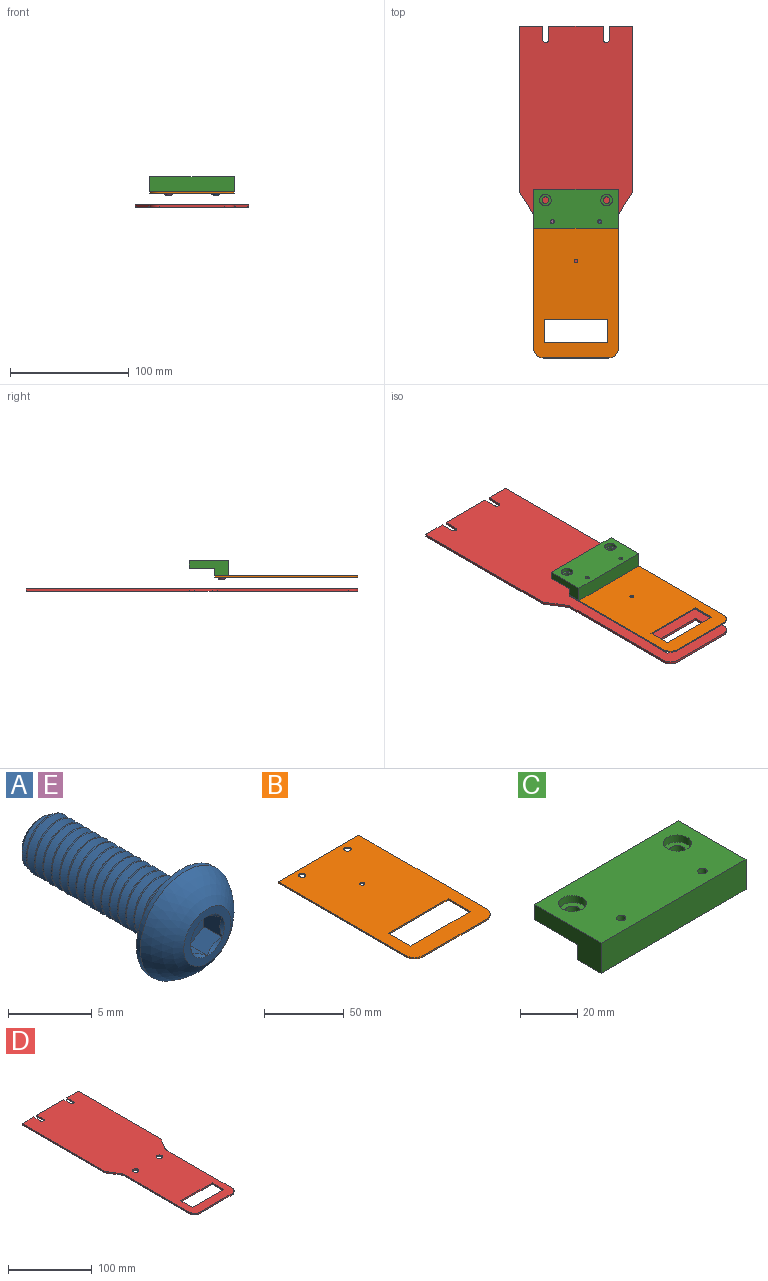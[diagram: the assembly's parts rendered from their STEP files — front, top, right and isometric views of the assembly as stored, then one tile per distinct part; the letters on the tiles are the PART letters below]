
ASSEMBLY  parts=5 mates=4
PART A: 24 faces, bbox 8.1x15x8.1 mm
  f0: cylinder r=2mm len=11.48mm, axis (0,1,0), area 2.5mm2, adj f2,f4,f6,f9
  f1: cone r=1.47mm half-angle=45deg, axis (0,-1,0), area 3.5mm2, adj f2,f3,f4,f5
  f2: cone r=1.47mm half-angle=45deg, axis (0,-1,0), area 0.9mm2, adj f0,f1,f4,f6
  f3: plane 2.95x2.95mm, normal (0,1,0), area 6.8mm2, adj f1
  f4: bspline ~12.61x4.62mm, area 97.8mm2, adj f0,f1,f2,f5,f9
  f5: cylinder r=1.55mm len=11.93mm, axis (0,1,0), area 17mm2, adj f1,f4,f6,f9
  f6: bspline ~12.4x4.62mm, area 97.9mm2, adj f0,f2,f5,f9
  f7: sphere r=4.23mm, area 49.7mm2, adj f8,f10
  f8: plane 4x4mm, normal (0,-1,0), area 6mm2, adj f7,f11,f12,f13,f14,f15,f16
  f9: plane 7.88x7.88mm, normal (0,1,0), area 35.4mm2, adj f0,f4,f5,f6,f10
  f10: cylinder r=3.8mm len=7.6mm, axis (0,-1,0), area 7.9mm2, adj f7,f9
  f11: cone r=1.44mm half-angle=45deg, axis (0,-1,0), area 0mm2, adj f8,f18
  f12: cone r=1.44mm half-angle=45deg, axis (0,-1,0), area 0mm2, adj f8,f19
  f13: cone r=1.44mm half-angle=45deg, axis (0,-1,0), area 0mm2, adj f8,f20
  f14: cone r=1.44mm half-angle=45deg, axis (0,-1,0), area 0mm2, adj f8,f21
  f15: cone r=1.44mm half-angle=45deg, axis (0,-1,0), area 0mm2, adj f8,f22
  f16: cone r=1.44mm half-angle=45deg, axis (0,-1,0), area 0mm2, adj f8,f23
  f17: plane 2.89x2.5mm, normal (0,-1,0), area 5.4mm2, adj f18,f19,f20,f21,f22,f23
  f18: plane 2.09x1.99mm, normal (-1,0,0), area 2mm2, adj f11,f17,f19,f23
  f19: plane 2.09x1.8mm, normal (-0.5,0,-0.87), area 2mm2, adj f12,f17,f18,f20
  f20: plane 2.09x1.8mm, normal (0.5,0,-0.87), area 2mm2, adj f13,f17,f19,f21
  f21: plane 2.09x1.99mm, normal (1,0,0), area 2mm2, adj f14,f17,f20,f22
  f22: plane 2.09x1.8mm, normal (0.5,0,0.87), area 2mm2, adj f15,f17,f21,f23
  f23: plane 2.09x1.8mm, normal (-0.5,0,0.87), area 2mm2, adj f16,f17,f18,f22
PART B: 15 faces, bbox 71.4x120.7x1 mm
  f0: plane 71.4x1mm, normal (0,1,0), area 71.4mm2, adj f1,f10,f11,f12
  f1: plane 112.7x1mm, normal (-1,0,0), area 112.7mm2, adj f0,f2,f11,f12
  f2: cylinder r=8mm len=8mm, axis (0,0,-1), area 12.6mm2, adj f1,f3,f11,f12
  f3: plane 55.4x1mm, normal (0,-1,0), area 55.4mm2, adj f2,f4,f11,f12
  f4: cylinder r=8mm len=8mm, axis (0,0,-1), area 12.6mm2, adj f3,f10,f11,f12
  f5: plane 52.8x1mm, normal (0,-1,0), area 52.8mm2, adj f6,f9,f11,f12
  f6: plane 19.6x1mm, normal (-1,0,0), area 19.6mm2, adj f5,f7,f11,f12
  f7: plane 52.8x1mm, normal (0,1,0), area 52.8mm2, adj f6,f9,f11,f12
  f8: cylinder r=1.5mm len=3mm, axis (0,0,-1), area 9.4mm2, adj f11,f12
  f9: plane 19.6x1mm, normal (1,0,0), area 19.6mm2, adj f5,f7,f11,f12
  f10: plane 112.7x1mm, normal (1,0,0), area 112.7mm2, adj f0,f4,f11,f12
  f11: plane 120.7x71.4mm, normal (0,0,1), area 7516.8mm2, adj f0,f1,f2,f3,f4,f5,f6,f7
  f12: plane 120.7x71.4mm, normal (0,0,-1), area 7516.8mm2, adj f0,f1,f2,f3,f4,f5,f6,f7
  f13: cylinder r=2.25mm len=4.5mm, axis (0,0,-1), area 14.1mm2, adj f11,f12
  f14: cylinder r=2.25mm len=4.5mm, axis (0,0,-1), area 14.1mm2, adj f11,f12
PART C: 16 faces, bbox 71.4x33x12.8 mm
  f0: plane 71.4x6.4mm, normal (0,1,0), area 457mm2, adj f1,f5,f6,f7
  f1: plane 71.4x21.5mm, normal (0,0,-1), area 1487.6mm2, adj f0,f2,f6,f7,f8,f11
  f2: plane 71.4x6.4mm, normal (0,1,0), area 457mm2, adj f1,f3,f6,f7
  f3: plane 71.4x33mm, normal (0,0,1), area 2189.8mm2, adj f2,f4,f6,f7,f10,f13,f14,f15
  f4: plane 71.4x12.8mm, normal (0,-1,0), area 913.9mm2, adj f3,f5,f6,f7
  f5: plane 71.4x11.5mm, normal (0,0,-1), area 804mm2, adj f0,f4,f6,f7,f14,f15
  f6: plane 33x12.8mm, normal (1,0,0), area 284.8mm2, adj f0,f1,f2,f3,f4,f5
  f7: plane 33x12.8mm, normal (-1,0,0), area 284.8mm2, adj f0,f1,f2,f3,f4,f5
  f8: cylinder r=2.75mm len=5.5mm, axis (0,0,1), area 58.7mm2, adj f1,f9
  f9: plane 9.75x9.75mm, normal (0,0,1), area 50.9mm2, adj f8,f10
  f10: cylinder r=4.88mm len=9.75mm, axis (0,0,1), area 91.9mm2, adj f3,f9
  f11: cylinder r=2.75mm len=5.5mm, axis (0,0,1), area 58.7mm2, adj f1,f12
  f12: plane 9.75x9.75mm, normal (0,0,1), area 50.9mm2, adj f11,f13
  f13: cylinder r=4.88mm len=9.75mm, axis (0,0,1), area 91.9mm2, adj f3,f12
  f14: cylinder r=1.65mm len=12.8mm, axis (0,0,1), area 132.7mm2, adj f3,f5
  f15: cylinder r=1.65mm len=12.8mm, axis (0,0,1), area 132.7mm2, adj f3,f5
PART D: 30 faces, bbox 95.4x280x2 mm
  f0: plane 46x2mm, normal (0,1,0), area 92mm2, adj f18,f19,f21,f22
  f1: plane 19.7x2mm, normal (0,1,0), area 39.4mm2, adj f16,f18,f19,f20
  f2: plane 52.8x2mm, normal (0,-1,0), area 105.6mm2, adj f3,f17,f18,f19
  f3: plane 19.6x2mm, normal (-1,0,0), area 39.2mm2, adj f2,f4,f18,f19
  f4: plane 52.8x2mm, normal (0,1,0), area 105.6mm2, adj f3,f17,f18,f19
  f5: plane 19.7x2mm, normal (0,1,0), area 39.4mm2, adj f6,f18,f19,f23
  f6: plane 137.69x2mm, normal (-1,0,0), area 275.4mm2, adj f5,f7,f18,f19
  f7: cylinder r=8mm len=4.27mm, axis (0,0,-1), area 9mm2, adj f6,f8,f18,f19
  f8: plane 15.09x9.53mm, normal (-0.85,-0.53,0), area 35.7mm2, adj f7,f18,f19,f24
  f9: plane 110.69x2mm, normal (-1,0,0), area 221.4mm2, adj f10,f18,f19,f24
  f10: cylinder r=8mm len=8mm, axis (0,0,-1), area 25.1mm2, adj f9,f11,f18,f19
  f11: plane 55.4x2mm, normal (0,-1,0), area 110.8mm2, adj f10,f12,f18,f19
  f12: cylinder r=8mm len=8mm, axis (0,0,-1), area 25.1mm2, adj f11,f13,f18,f19
  f13: plane 110.69x2mm, normal (1,0,0), area 221.4mm2, adj f12,f18,f19,f25
  f14: plane 15.09x9.53mm, normal (0.85,-0.53,0), area 35.7mm2, adj f15,f18,f19,f25
  f15: cylinder r=8mm len=4.27mm, axis (0,0,-1), area 9mm2, adj f14,f16,f18,f19
  f16: plane 137.69x2mm, normal (1,0,0), area 275.4mm2, adj f1,f15,f18,f19
  f17: plane 19.6x2mm, normal (1,0,0), area 39.2mm2, adj f2,f4,f18,f19
  f18: plane 280x95.4mm, normal (0,0,1), area 22292.3mm2, adj f0,f1,f2,f3,f4,f5,f6,f7
  f19: plane 280x95.4mm, normal (0,0,-1), area 22292.3mm2, adj f0,f1,f2,f3,f4,f5,f6,f7
  f20: plane 11.5x2mm, normal (-1,0,0), area 23mm2, adj f1,f18,f19,f26
  f21: plane 11.5x2mm, normal (1,0,0), area 23mm2, adj f0,f18,f19,f26
  f22: plane 11.5x2mm, normal (-1,0,0), area 23mm2, adj f0,f18,f19,f27
  f23: plane 11.5x2mm, normal (1,0,0), area 23mm2, adj f5,f18,f19,f27
  f24: cylinder r=8mm len=4.27mm, axis (0,0,-1), area 9mm2, adj f8,f9,f18,f19
  f25: cylinder r=8mm len=4.27mm, axis (0,0,-1), area 9mm2, adj f13,f14,f18,f19
  f26: cylinder r=2.5mm len=5mm, axis (0,0,1), area 15.7mm2, adj f18,f19,f20,f21
  f27: cylinder r=2.5mm len=5mm, axis (0,0,1), area 15.7mm2, adj f18,f19,f22,f23
  f28: cylinder r=3.8mm len=7.6mm, axis (0,0,1), area 47.8mm2, adj f18,f19
  f29: cylinder r=3.8mm len=7.6mm, axis (0,0,1), area 47.8mm2, adj f18,f19
PART E: same geometry as A
PLACE A rot(axis=(1,0,0),90deg) t=(22.71,-5.75,-22.44)mm
PLACE B t=(-32.96,0.05,-20.24)mm
PLACE C t=(-32.96,-5.7,-12.84)mm
PLACE D t=(-32.96,159.35,-32.24)mm
PLACE E rot(axis=(1,0,0),90deg) t=(-17.26,-5.7,-22.44)mm
MATE fastened B.f11 <-> C.f5  axis (0,0,1) through (38.44,0.05,-19.24)mm
MATE fastened B.f10 <-> D.f13  axis (1,0,0) through (38.44,-112.65,-20.24)mm
MATE fastened A.f9 <-> B.f13  axis (0,0,1) through (22.74,-5.7,-20.24)mm
MATE fastened E.f10 <-> B.f14  axis (0,0,1) through (-17.26,-5.7,-20.24)mm
